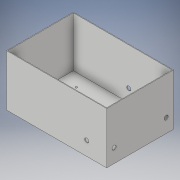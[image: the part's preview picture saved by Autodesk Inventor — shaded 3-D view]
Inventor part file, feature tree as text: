
AUTODESK INVENTOR PART (.ipt)
format: ipt  version: 2018 (Build 220112000, 112)  size: 165,376 bytes
history: native  units: in
note: dims shown in document units (in); Inventor stores cm internally (conversion verified against a paired STEP export)
features: extrude x7, sketch x7
ambient origin geometry x8: Origin, YZ Plane, XZ Plane, XY Plane, X Axis, Y Axis, Z Axis, Center Point
bodies: Solid1 (feature_tree)
feature tree (14):
  extrude  "Extrusion1"  Depth=4.0in
  extrude  "Extrusion2"  Depth=5.92in
  extrude  "Extrusion3"  Depth=3.0in TaperAngle=0.0deg
  extrude  "Extrusion4"  Depth=0.164in
  extrude  "Extrusion5"  Depth=2.598in
  extrude  "Extrusion6"  Depth=0.118in
  extrude  "Extrusion7"  Depth=0.125in
  sketch  "Sketch1"  dims[d0=6.0in d1=4.0in]
  sketch  "Sketch2"  dims[d2=0.08in d3=0.0in d4=5.92in]
  sketch  "Sketch3"  dims[d5=3.92in d6=3.0in d7=0.0in]
  sketch  "Sketch4"  dims[d10=0.164in d11=0.164in]
  sketch  "Sketch5"  dims[d12=0.0in d13=0.0in d14=2.598in]
  sketch  "Sketch6"  dims[d15=0.787in d16=0.118in]
  sketch  "Sketch7"  dims[d17=0.118in d18=0.118in d19=0.118in d20=5.512in d21=2.1875in d34=0.0in d35=0.0in d39=0.25in d40=0.25in d41=0.25in d42=0.0in d43=0.0in d44=0.25in d45=0.25in d46=0.0in d47=0.0in d51=0.25in d52=1.0in d53=0.0in d55=0.125in d57=0.125in d59=0.125in d61=0.125in]
